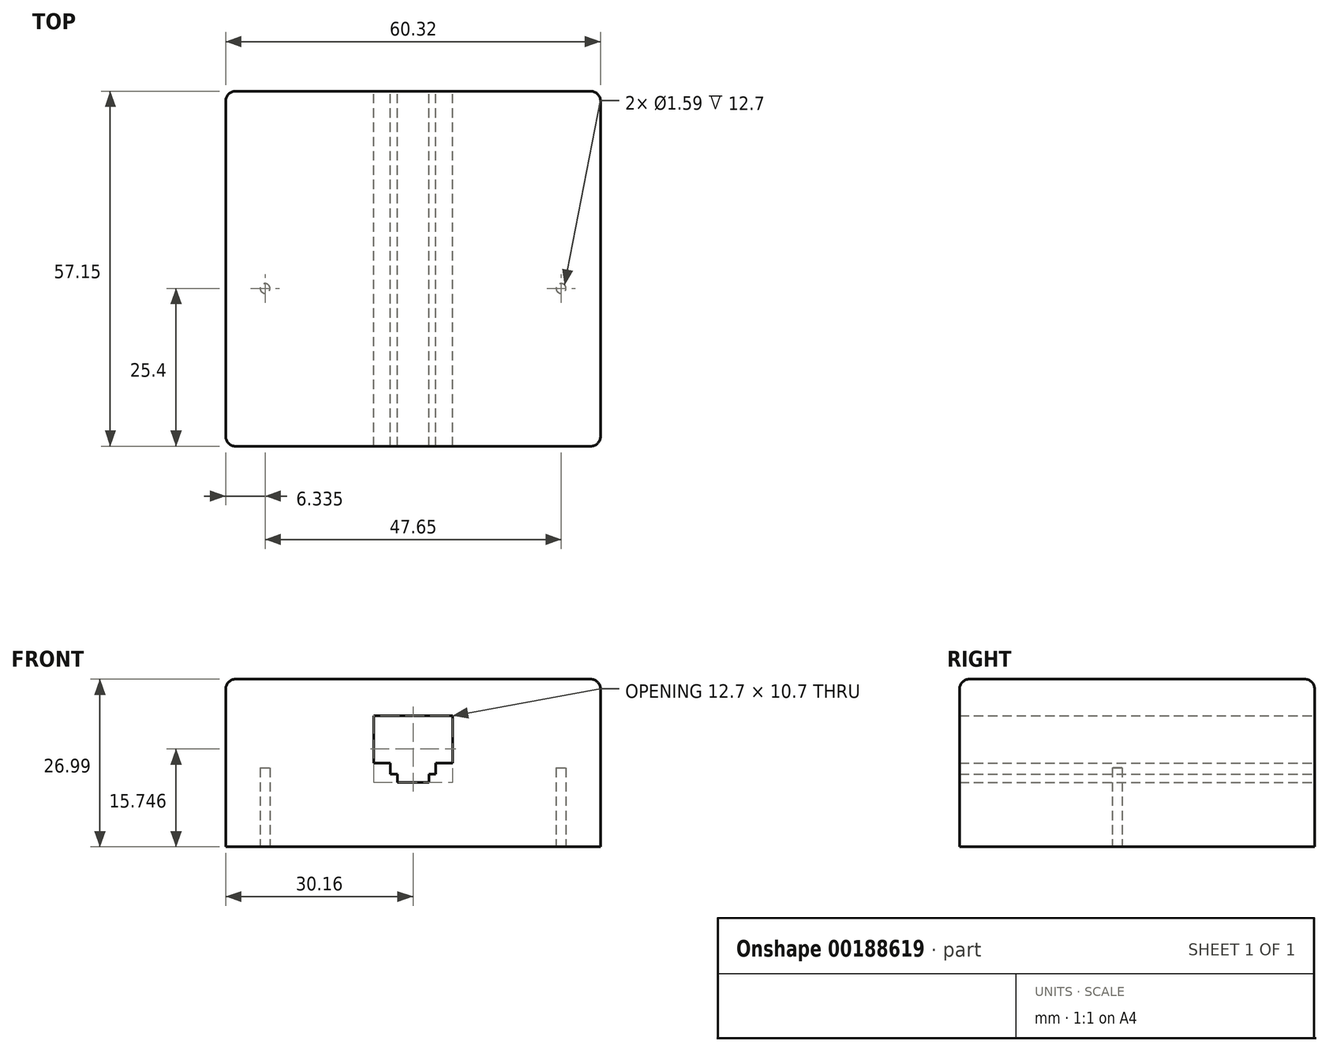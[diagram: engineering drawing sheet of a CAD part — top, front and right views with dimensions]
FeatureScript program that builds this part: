
annotation { "Feature Type Name" : "Feature", "Feature Type Description" : "" }
export const myFeature = defineFeature(function(context is Context, id is Id, definition is map)
    precondition{}
    {
        {
            var Q0;
            Q0=qCreatedBy(makeId("Front.planeOp"),FACE);
            var sketch = newSketch(context, id + "F0", { "sketchPlane" : qUnion([Q0])});
            skLineSegment(sketch, "E0", {"start": v(6.35, 5.1) * mm, "end": v(-6.35, 5.1) * mm});
            skLineSegment(sketch, "E1", {"start": v(-6.35, 5.1) * mm, "end": v(-6.35, -2.5) * mm});
            skLineSegment(sketch, "E2", {"start": v(-6.35, -2.5) * mm, "end": v(-3.65, -2.5) * mm});
            skLineSegment(sketch, "E3", {"start": v(-3.65, -2.5) * mm, "end": v(-3.65, -4.3) * mm});
            skLineSegment(sketch, "E4", {"start": v(-3.65, -4.3) * mm, "end": v(-2.55, -4.3) * mm});
            skLineSegment(sketch, "E5", {"start": v(-2.55, -4.3) * mm, "end": v(-2.55, -5.6) * mm});
            skLineSegment(sketch, "E6", {"start": v(-2.55, -5.6) * mm, "end": v(2.55, -5.6) * mm});
            skLineSegment(sketch, "E7", {"start": v(2.55, -5.6) * mm, "end": v(2.55, -4.3) * mm});
            skLineSegment(sketch, "E8", {"start": v(2.55, -4.3) * mm, "end": v(3.65, -4.3) * mm});
            skLineSegment(sketch, "E9", {"start": v(3.65, -4.3) * mm, "end": v(3.65, -2.5) * mm});
            skLineSegment(sketch, "E10", {"start": v(3.65, -2.5) * mm, "end": v(6.35, -2.5) * mm});
            skLineSegment(sketch, "E11", {"start": v(6.35, -2.5) * mm, "end": v(6.35, 5.1) * mm});
            skLineSegment(sketch, "E12.bottom", {"start": v(-30.16, 11) * mm, "end": v(30.16, 11) * mm});
            skLineSegment(sketch, "E12.top", {"start": v(-30.16, -15.99) * mm, "end": v(30.16, -15.99) * mm});
            skLineSegment(sketch, "E12.left", {"start": v(-30.16, 11) * mm, "end": v(-30.16, -15.99) * mm});
            skLineSegment(sketch, "E12.right", {"start": v(30.16, 11) * mm, "end": v(30.16, -15.99) * mm});
            skPoint(sketch, "E13", {"position": v(0, 5.1) * mm});
            skPoint(sketch, "E14", {"position": v(0, -15.99) * mm});
            skPoint(sketch, "E15", {"position": v(30.16, -2.5) * mm});
            skLineSegment(sketch, "E16", {"start": v(0, 5.1) * mm, "end": v(0, -15.99) * mm, "construction": true});
            skSolve(sketch);
        }
        {
            var Q0;
            Q0=makeQuery(id+"F0.imprint","IMPRINT",FACE,{"disambiguationData":[TD([[makeQuery(id+"F0.imprint","IMPRINT",EDGE,{"derivedFrom":sQuery(id+"F0.wireOp",EDGE,"E0")}),-1.0]])]});
            extrude(context, id + "F1", {"entities" : qUnion([Q0]), "depth" : 57.15 * mm});
        }
        {
            var Q0;
            Q0=makeQuery(id+"F1.opExtrude","SWEPT_EDGE",EDGE,{"disambiguationData":[OSD([sQuery(id+"F0.wireOp",EDGE,"E12.bottom"),sQuery(id+"F0.wireOp",EDGE,"E12.left")])]});
            var Q1;
            Q1=makeQuery(id+"F1.opExtrude","CAP_EDGE",EDGE,{"disambiguationData":[OSD([sQuery(id+"F0.wireOp",EDGE,"E12.bottom")])],"isStart":false});
            var Q2;
            Q2=makeQuery(id+"F1.opExtrude","CAP_EDGE",EDGE,{"disambiguationData":[OSD([sQuery(id+"F0.wireOp",EDGE,"E12.left")])],"isStart":false});
            var Q3;
            Q3=makeQuery(id+"F1.opExtrude","CAP_EDGE",EDGE,{"disambiguationData":[OSD([sQuery(id+"F0.wireOp",EDGE,"E12.left")])],"isStart":true});
            var Q4;
            Q4=makeQuery(id+"F1.opExtrude","CAP_EDGE",EDGE,{"disambiguationData":[OSD([sQuery(id+"F0.wireOp",EDGE,"E12.bottom")])],"isStart":true});
            var Q5;
            Q5=makeQuery(id+"F1.opExtrude","SWEPT_EDGE",EDGE,{"disambiguationData":[OSD([sQuery(id+"F0.wireOp",EDGE,"E12.bottom"),sQuery(id+"F0.wireOp",EDGE,"E12.right")])]});
            var Q6;
            Q6=makeQuery(id+"F1.opExtrude","CAP_EDGE",EDGE,{"disambiguationData":[OSD([sQuery(id+"F0.wireOp",EDGE,"E12.right")])],"isStart":true});
            var Q7;
            Q7=makeQuery(id+"F1.opExtrude","CAP_EDGE",EDGE,{"disambiguationData":[OSD([sQuery(id+"F0.wireOp",EDGE,"E12.right")])],"isStart":false});
            fillet(context, id + "F2", {"entities" : qUnion([Q0, Q1, Q2, Q3, Q4, Q5, Q6, Q7]), "radius" : 1.59 * mm, "tangentPropagation" : true, "allowEdgeOverflow" : false});
        }
        {
            var Q0;
            Q0=makeQuery(id+"F1.opExtrude","SWEPT_FACE",FACE,{"disambiguationData":[OSD([sQuery(id+"F0.wireOp",EDGE,"E12.top")])]});
            var sketch = newSketch(context, id + "F3", { "sketchPlane" : qUnion([Q0])});
            skLineSegment(sketch, "E17", {"start": v(0, 57.15) * mm, "end": v(0, 0) * mm, "construction": true});
            skLineSegment(sketch, "E18", {"start": v(30.16, 28.58) * mm, "end": v(-30.16, 28.58) * mm, "construction": true});
            skPoint(sketch, "E19", {"position": v(0, 31.75) * mm});
            skLineSegment(sketch, "E20", {"start": v(0, 31.75) * mm, "end": v(23.83, 31.75) * mm, "construction": true});
            skLineSegment(sketch, "E21", {"start": v(0, 31.75) * mm, "end": v(-23.83, 31.75) * mm, "construction": true});
            skCircle(sketch, "E22", {"center": v(-23.83, 31.75) * mm, "radius": 0.8 * mm});
            skCircle(sketch, "E23", {"center": v(23.83, 31.75) * mm, "radius": 0.8 * mm});
            skSolve(sketch);
        }
        {
            var Q0;
            Q0=makeQuery(id+"F3.imprint","IMPRINT",FACE,{"disambiguationData":[TD([[makeQuery(id+"F3.imprint","IMPRINT",EDGE,{"derivedFrom":sQuery(id+"F3.wireOp",EDGE,"E23")}),1.0]])]});
            var Q1;
            Q1=makeQuery(id+"F3.imprint","IMPRINT",FACE,{"disambiguationData":[TD([[makeQuery(id+"F3.imprint","IMPRINT",EDGE,{"derivedFrom":sQuery(id+"F3.wireOp",EDGE,"E22")}),1.0]])]});
            extrude(context, id + "F4", {"entities" : qUnion([Q0, Q1]), "operationType" : NewBodyOperationType.REMOVE, "oppositeDirection" : true, "depth" : 12.7 * mm});
        }
    });
